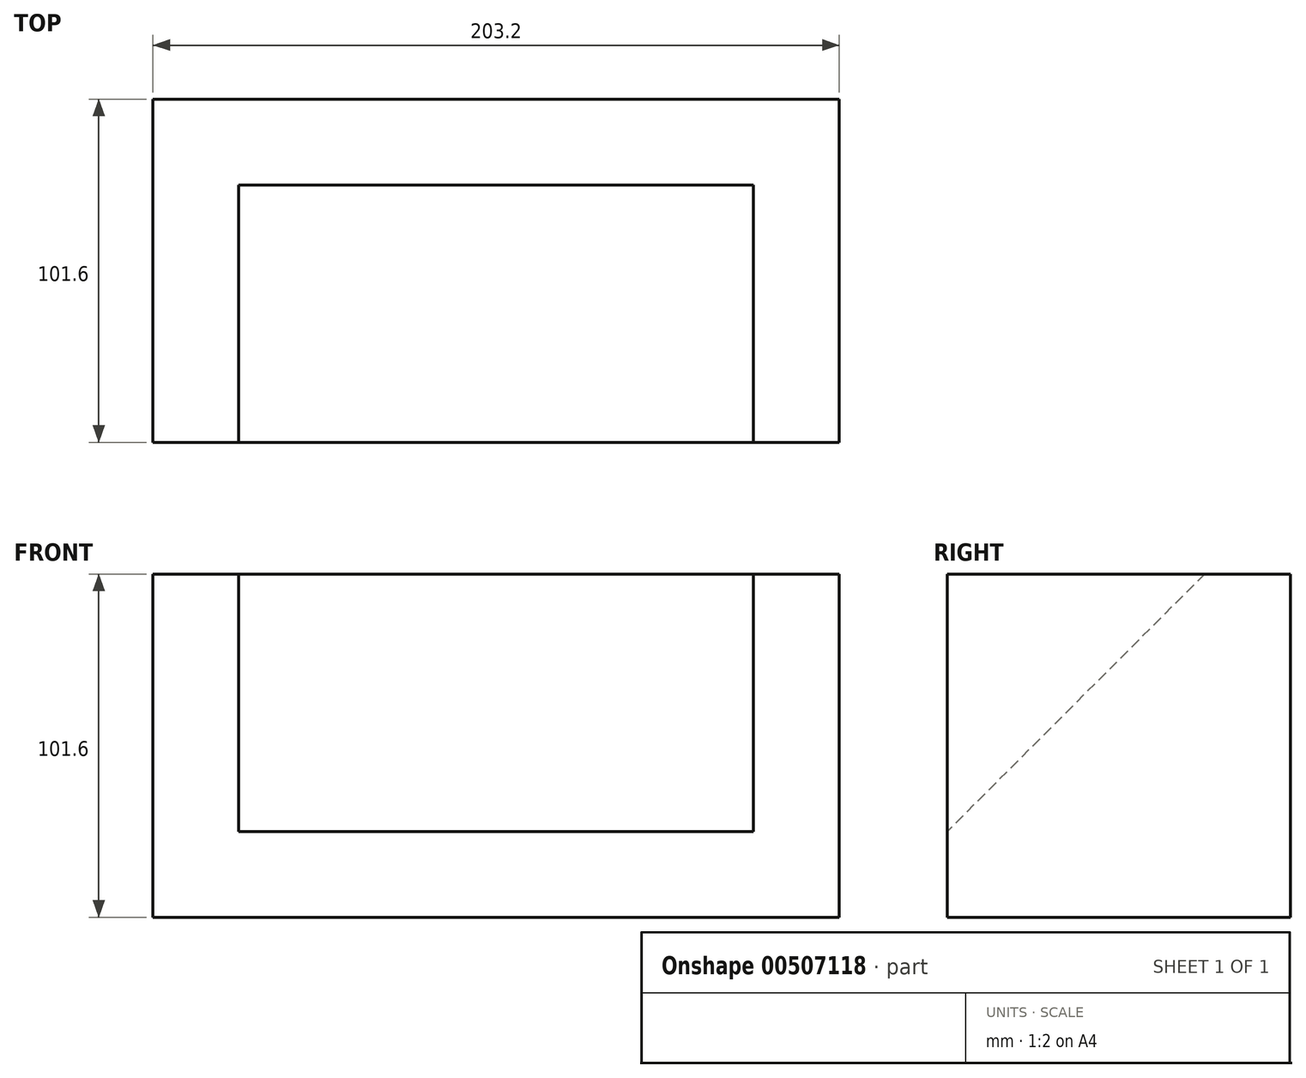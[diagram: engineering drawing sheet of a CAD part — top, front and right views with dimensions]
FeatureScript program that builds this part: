
annotation { "Feature Type Name" : "Feature", "Feature Type Description" : "" }
export const myFeature = defineFeature(function(context is Context, id is Id, definition is map)
    precondition{}
    {
        {
            var Q0;
            Q0=qCreatedBy(makeId("Top.planeOp"),FACE);
            var sketch = newSketch(context, id + "F0", { "sketchPlane" : qUnion([Q0])});
            skLineSegment(sketch, "E0.bottom", {"start": v(101.6, 50.8) * mm, "end": v(-101.6, 50.8) * mm});
            skLineSegment(sketch, "E0.top", {"start": v(101.6, -50.8) * mm, "end": v(-101.6, -50.8) * mm});
            skLineSegment(sketch, "E0.left", {"start": v(101.6, 50.8) * mm, "end": v(101.6, -50.8) * mm});
            skLineSegment(sketch, "E0.right", {"start": v(-101.6, 50.8) * mm, "end": v(-101.6, -50.8) * mm});
            skPoint(sketch, "E0.middle", {"position": v(0, 0) * mm});
            skSolve(sketch);
        }
        {
            var Q0;
            Q0 = qSketchRegion(id + "F0", true);
            extrude(context, id + "F1", {"entities" : qUnion([Q0]), "depth" : 101.6 * mm});
        }
        {
            var Q0;
            Q0=makeQuery(id+"F1.opExtrude","CAP_FACE",FACE,{"disambiguationData":[OSD([sQuery(id+"F0.wireOp",EDGE,"E0.bottom"),sQuery(id+"F0.wireOp",EDGE,"E0.top"),sQuery(id+"F0.wireOp",EDGE,"E0.left"),sQuery(id+"F0.wireOp",EDGE,"E0.right")])],"isStart":false});
            var sketch = newSketch(context, id + "F2", { "sketchPlane" : qUnion([Q0])});
            skLineSegment(sketch, "E1.bottom", {"start": v(-76.2, -50.8) * mm, "end": v(76.2, -50.8) * mm});
            skLineSegment(sketch, "E1.top", {"start": v(-76.2, 25.4) * mm, "end": v(76.2, 25.4) * mm});
            skLineSegment(sketch, "E1.left", {"start": v(-76.2, -50.8) * mm, "end": v(-76.2, 25.4) * mm});
            skLineSegment(sketch, "E1.right", {"start": v(76.2, -50.8) * mm, "end": v(76.2, 25.4) * mm});
            skSolve(sketch);
        }
        {
            var Q0;
            Q0 = qSketchRegion(id + "F2", true);
            extrude(context, id + "F3", {"entities" : qUnion([Q0]), "operationType" : NewBodyOperationType.REMOVE, "oppositeDirection" : true, "depth" : 76.2 * mm});
        }
        {
            var Q0;
            Q0=makeQuery(id+"F3.boolean.opBoolean","COPY",FACE,{"derivedFrom":makeQuery(id+"F3.opExtrude","SWEPT_FACE",FACE,{"disambiguationData":[OSD([sQuery(id+"F2.wireOp",EDGE,"E1.left")])]})});
            var sketch = newSketch(context, id + "F4", { "sketchPlane" : qUnion([Q0])});
            skLineSegment(sketch, "E2", {"start": v(25.4, 101.6) * mm, "end": v(-50.8, 25.4) * mm});
            skLineSegment(sketch, "E3", {"start": v(-50.8, 25.4) * mm, "end": v(25.4, 25.4) * mm});
            skLineSegment(sketch, "E4", {"start": v(25.4, 25.4) * mm, "end": v(25.4, 101.6) * mm});
            skSolve(sketch);
        }
        {
            var Q0;
            Q0=makeQuery(id+"F4.imprint","IMPRINT",FACE,{"disambiguationData":[TD([[makeQuery(id+"F4.imprint","IMPRINT",EDGE,{"derivedFrom":sQuery(id+"F4.wireOp",EDGE,"E2")}),1.0]])]});
            extrude(context, id + "F5", {"entities" : qUnion([Q0]), "operationType" : NewBodyOperationType.ADD, "depth" : 152.4 * mm});
        }
    });
